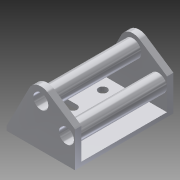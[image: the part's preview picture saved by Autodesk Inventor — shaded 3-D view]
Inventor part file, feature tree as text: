
AUTODESK INVENTOR PART (.ipt)
format: ipt  version: 2015 SP1 (Build 190203100, 203)  size: 291,328 bytes
history: native  units: in
note: dims shown in document units (in); Inventor stores cm internally (conversion verified against a paired STEP export)
features: extrude x7, sketch x7, projected_geometry x6
ambient origin geometry x8: Origin, YZ Plane, XZ Plane, XY Plane, X Axis, Y Axis, Z Axis, Center Point
bodies: Solid1 (feature_tree)
feature tree (20):
  extrude  "Extrusion1"  Depth=2.5in
  extrude  "Extrusion2"  Depth=2.0in
  extrude  "Extrusion3"  Depth=0.25in
  extrude  "Extrusion5"  Depth=0.25in
  extrude  "Extrusion6"  TaperAngle=0.0deg  [1 undecoded]
  extrude  "Extrusion7"  TaperAngle=0.0deg  [1 undecoded]
  extrude  "Extrusion8"  Depth=0.25in
  sketch  "Sketch1"  dims[d0=3.0in d1=2.5in]
  sketch  "Sketch2"  dims[d2=1.75in d3=2.0in]
  projected_geometry  "Projected Loop1"
  sketch  "Sketch3"  dims[d4=0.25in d5=0.25in]
  projected_geometry  "Projected Loop2"
  projected_geometry  "Projected Loop3"
  sketch  "Sketch5"  dims[d6=0.25in d7=0.5in]
  projected_geometry  "Projected Loop5"
  sketch  "Sketch6"  dims[d8=0.25in d9=0.0in]
  projected_geometry  "Projected Loop6"
  sketch  "Sketch7"  dims[d10=0.0in d11=0.0in]
  projected_geometry  "Projected Loop7"
  sketch  "Sketch8"  dims[d12=0.0in d13=0.25in d14=0.25in d15=0.5in d16=0.0in d17=0.25in d18=0.25in d19=0.0in d20=0.5in d21=0.125in d22=0.0in d23=0.4375in d24=1.25in d25=1.0in d26=0.4375in d27=0.75in d28=1.25in d29=0.375in d30=0.1875in d31=0.0in d32=0.1875in d33=0.0in d38=0.5in d39=0.5in d40=2.5in d41=0.0in d42=0.25in d43=0.25in d44=0.25in d45=0.25in d46=0.25in d47=0.25in d50=0.875in d51=0.875in d52=0.0in d53=0.0in d54=0.0in d55=0.5in d56=0.5in d57=0.0in d58=0.0in d59=0.0in d60=0.875in d61=0.875in d62=2.5in d63=0.0in d64=1.0in d65=3.25in d66=3.0in d67=2.5in d68=0.0in d69=2.5in d70=2.5in d71=1.0in d72=0.0in]
note: 2 required parameter values undecoded (feature->parameter linkage not recoverable at this tier; creation-order binding heuristic only, values carry confidence <= 0.55)
